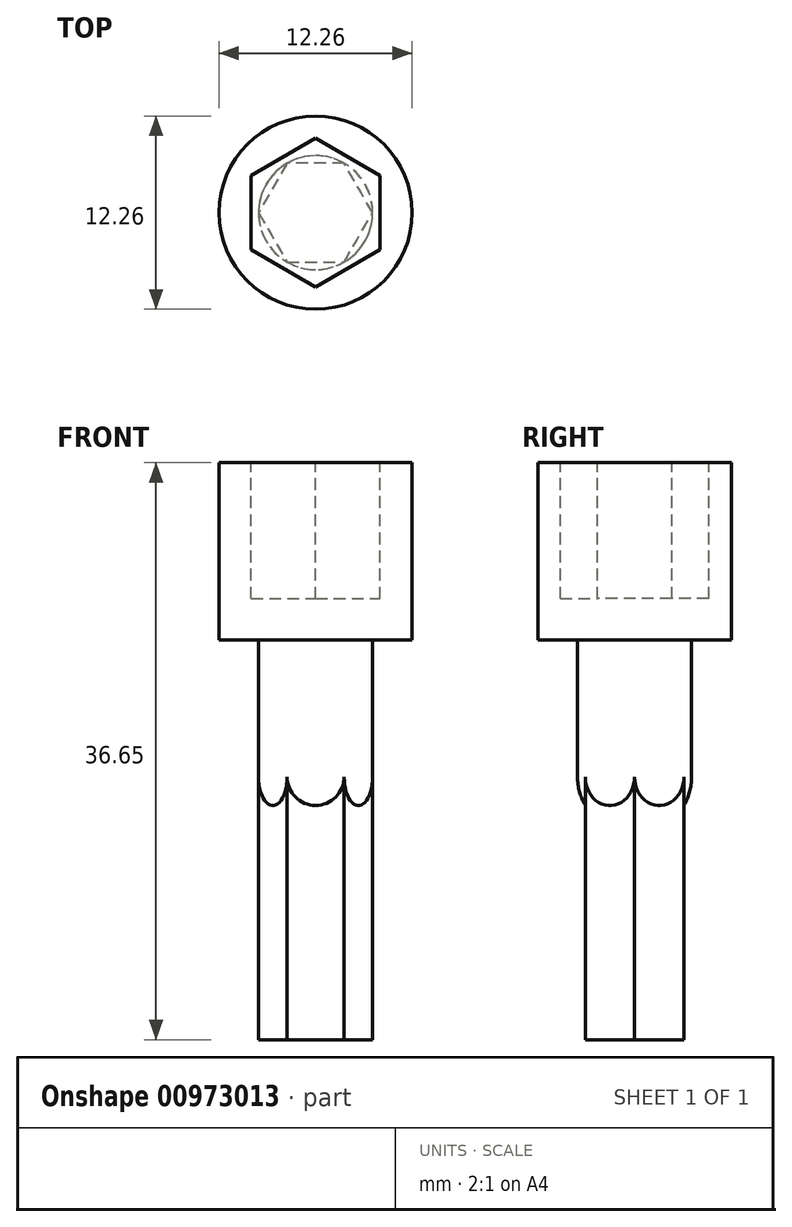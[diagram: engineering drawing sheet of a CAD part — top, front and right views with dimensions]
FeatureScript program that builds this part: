
annotation { "Feature Type Name" : "Feature", "Feature Type Description" : "" }
export const myFeature = defineFeature(function(context is Context, id is Id, definition is map)
    precondition{}
    {
        {
            var Q0;
            Q0=qCreatedBy(makeId("Top.planeOp"),FACE);
            var sketch = newSketch(context, id + "F0", { "sketchPlane" : qUnion([Q0])});
            skCircle(sketch, "E0", {"center": v(0, 0) * mm, "radius": 6.13 * mm});
            skSolve(sketch);
        }
        {
            var Q0;
            Q0=qSketchRegion(id+"F0",true);
            extrude(context, id + "F1", {"entities" : qUnion([Q0]), "depth" : 11.25 * mm, "offsetDistance" : 25.4 * mm});
        }
        {
            var Q0;
            Q0=makeQuery(id+"F1.opExtrude","CAP_FACE",FACE,{"disambiguationData":[OSD([sQuery(id+"F0.wireOp",EDGE,"E0")])],"isStart":false});
            var sketch = newSketch(context, id + "F2", { "sketchPlane" : qUnion([Q0])});
            skCircle(sketch, "E1.cCircle", {"center": v(0, 0) * mm, "radius": 4.09 * mm, "construction": true});
            skLineSegment(sketch, "E1.0", {"start": v(4.09, 2.36) * mm, "end": v(4.09, -2.36) * mm});
            skLineSegment(sketch, "E1.1", {"start": v(4.09, -2.36) * mm, "end": v(0, -4.72) * mm});
            skLineSegment(sketch, "E1.2", {"start": v(0, -4.72) * mm, "end": v(-4.09, -2.36) * mm});
            skLineSegment(sketch, "E1.3", {"start": v(-4.09, -2.36) * mm, "end": v(-4.09, 2.36) * mm});
            skLineSegment(sketch, "E1.4", {"start": v(-4.09, 2.36) * mm, "end": v(0, 4.72) * mm});
            skLineSegment(sketch, "E1.5", {"start": v(0, 4.72) * mm, "end": v(4.09, 2.36) * mm});
            skPoint(sketch, "E1.0.midPoint", {"position": v(4.09, 0) * mm});
            skSolve(sketch);
        }
        {
            var Q0;
            Q0=qSketchRegion(id+"F2",true);
            var Q1;
            Q1=makeQuery(id+"F2.imprint","IMPRINT",FACE,{"disambiguationData":[TD([[makeQuery(id+"F2.imprint","IMPRINT",EDGE,{"derivedFrom":sQuery(id+"F2.wireOp",EDGE,"E1.0")}),-1.0]])]});
            extrude(context, id + "F3", {"entities" : qUnion([Q0, Q1]), "operationType" : NewBodyOperationType.REMOVE, "oppositeDirection" : true, "depth" : 8.64 * mm, "offsetDistance" : 25.4 * mm});
        }
        {
            var Q0;
            Q0=makeQuery(id+"F1.opExtrude","CAP_FACE",FACE,{"disambiguationData":[OSD([sQuery(id+"F0.wireOp",EDGE,"E0")])],"isStart":true});
            var sketch = newSketch(context, id + "F4", { "sketchPlane" : qUnion([Q0])});
            skCircle(sketch, "E2.cCircle", {"center": v(0, 0) * mm, "radius": 3.14 * mm, "construction": true});
            skLineSegment(sketch, "E2.0", {"start": v(1.81, -3.14) * mm, "end": v(-1.81, -3.14) * mm});
            skLineSegment(sketch, "E2.1", {"start": v(-1.81, -3.14) * mm, "end": v(-3.62, 0) * mm});
            skLineSegment(sketch, "E2.2", {"start": v(-3.62, 0) * mm, "end": v(-1.81, 3.14) * mm});
            skLineSegment(sketch, "E2.3", {"start": v(-1.81, 3.14) * mm, "end": v(1.81, 3.14) * mm});
            skLineSegment(sketch, "E2.4", {"start": v(1.81, 3.14) * mm, "end": v(3.62, 0) * mm});
            skLineSegment(sketch, "E2.5", {"start": v(3.62, 0) * mm, "end": v(1.81, -3.14) * mm});
            skPoint(sketch, "E2.0.midPoint", {"position": v(0, -3.14) * mm});
            skSolve(sketch);
        }
        {
            var Q0;
            Q0=makeQuery(id+"F4.imprint","IMPRINT",FACE,{"disambiguationData":[TD([[makeQuery(id+"F4.imprint","IMPRINT",EDGE,{"derivedFrom":sQuery(id+"F4.wireOp",EDGE,"E2.0")}),-1.0]])]});
            extrude(context, id + "F5", {"entities" : qUnion([Q0]), "operationType" : NewBodyOperationType.ADD, "depth" : 25.4 * mm, "offsetDistance" : 25.4 * mm});
        }
        {
            var Q0;
            Q0=qCreatedBy(makeId("Front.planeOp"),FACE);
            var sketch = newSketch(context, id + "F6", { "sketchPlane" : qUnion([Q0])});
            skPoint(sketch, "E3.0", {"position": v(-3.62, 0) * mm});
            skLineSegment(sketch, "E4.bottom", {"start": v(-3.62, 0) * mm, "end": v(0, 0) * mm});
            skLineSegment(sketch, "E4.left", {"start": v(-3.62, 0) * mm, "end": v(-3.62, -8.71) * mm});
            skArc(sketch, "E5", {"start": v(-3.62, -8.71) * mm, "mid": v(-2.56, -11.27) * mm, "end": v(0, -12.33) * mm});
            skLineSegment(sketch, "E6", {"start": v(0, 0) * mm, "end": v(0, -12.33) * mm});
            skSolve(sketch);
        }
        {
            var Q0;
            Q0=qSketchRegion(id+"F6",true);
            var Q1;
            Q1=sQuery(id+"F6.wireOp",EDGE,"E6");
            revolve(context, id + "F7", {"operationType" : NewBodyOperationType.ADD, "surfaceOperationType" : NewSurfaceOperationType.NEW, "entities" : qUnion([Q0]), "axis" : qUnion([Q1]), "revolveType" : RevolveType.FULL});
        }
    });
